# Revit family: 230009KCG01-076_KOEC530P
name_source: partatom
category: Specialty Equipment
units: mm (PartAtom-declared; Revit-internal decimal feet)

## family parameters
Always vertical = Yes
Cut with Voids When Loaded = No
Enable Cutting in Views = No
Maintain Annotation Orientation = No
Part Type = Normal
Room Calculation Point = No
Round Connector Dimension = Use Diameter
Shared = No
Work Plane-Based = No

## types (3) — shared parameters
Accent Material = ARCAT - Metal - Steel - Gray - Light
Apparent Load = 0 VA
Body Material = ARCAT - Metal - Steel - Stainless
Clearance Material = ARCAT - Clearance
Default Elevation = 0"
Depth = 27 1/8"
Description = KitchenAid® Combination Microwave Wall Ovens with Air Fry Mode
Display Panel Material = ARCAT - Glass - Black
Door Frame = ARCAT - Metal - Steel - Black Stainless
Door Front Panel Material = ARCAT - Metal - Steel - Stainless
Family Name = Combination Built-In Oven
Feature 1 = Air Fry Mode
Feature 2 = Dishwasher-Safe Air Fry Basket
Feature 3 = Even-Heat™ True Convection
Glass Material = ARCAT - Glass - Tempered - Black
Handle Material = ARCAT - Metal - Steel - Grey
Height = 42 1/2"
Ring = ARCAT - Metal - Steel - Red
Voltage = 0 V
Width = 29 3/4"

## per-type parameters (varying)
| type | Display Unit | Door Material | Style Master |
| KOEC530PSS | ARCAT - Metal - Steel - Black Stainless | ARCAT - Metal - Steel - Stainless - Light | ARCAT - Metal - Steel - Stainless - Light |
| KOEC530PBS | ARCAT - Metal - Steel - Black Stainless | ARCAT - Metal - Steel - Black | ARCAT - Metal - Steel - Black Stainless |
| KOEC530PWH | ARCAT - Metal - Steel - Gray - Light | ARCAT - Metal - Steel - Gray - Light | ARCAT - Metal - Steel - Gray - Light |

## geometry (parser evidence)
native form markers: Sweep x5
no freeform markers — native parametric forms only
